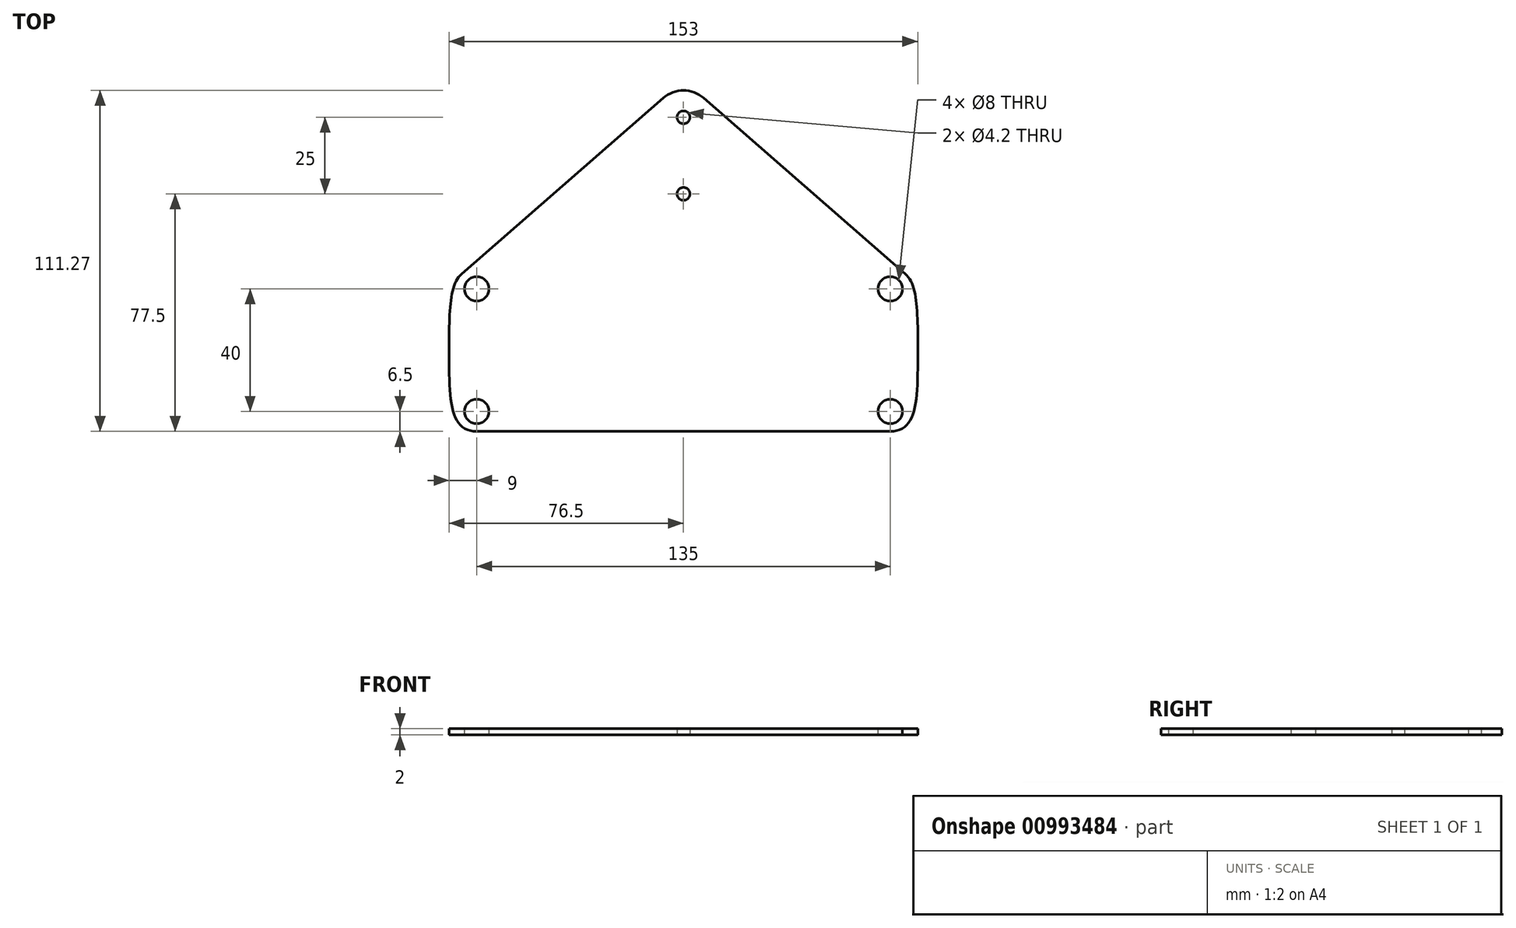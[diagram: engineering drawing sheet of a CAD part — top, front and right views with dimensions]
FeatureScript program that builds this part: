
annotation { "Feature Type Name" : "Feature", "Feature Type Description" : "" }
export const myFeature = defineFeature(function(context is Context, id is Id, definition is map)
    precondition{}
    {
        {
            var Q0;
            Q0=qCreatedBy(makeId("Top.planeOp"), FACE);
            var sketch = newSketch(context, id + "F0", { "sketchPlane" : qUnion([Q0])});
            skPoint(sketch, "E0", {"position": v(-67.5, 0) * mm});
            skPoint(sketch, "E1", {"position": v(-67.5, 40) * mm});
            skPoint(sketch, "E2", {"position": v(0, 71) * mm});
            skPoint(sketch, "E3", {"position": v(0, 96) * mm});
            skLineSegment(sketch, "E4", {"start": v(0, 0) * mm, "end": v(0, 32.96) * mm, "construction": true});
            skCircle(sketch, "E5", {"center": v(-67.5, 0) * mm, "radius": 4 * mm});
            skCircle(sketch, "E6", {"center": v(-67.5, 40) * mm, "radius": 4 * mm});
            skCircle(sketch, "E7", {"center": v(0, 71) * mm, "radius": 2.1 * mm});
            skCircle(sketch, "E8", {"center": v(0, 96) * mm, "radius": 2.1 * mm});
            skPoint(sketch, "E9", {"position": v(-67.5, 46.5) * mm});
            skPoint(sketch, "E10", {"position": v(-76.5, 20) * mm});
            skLineSegment(sketch, "E11", {"start": v(-67.5, 40) * mm, "end": v(-67.5, 0) * mm, "construction": true});
            skFitSpline(sketch, "E12", {"points": [v(-67.5, 46.5) * mm, v(-76.5, 20) * mm], "startDerivative": vector(-27, 0) * mm, "endDerivative": vector(0, -48) * mm});
            skLineSegment(sketch, "E13", {"start": v(-76.5, 20) * mm, "end": v(-53.05, 20) * mm, "construction": true});
            skLineSegment(sketch, "E14.bottom", {"start": v(-7.5, 101.5) * mm, "end": v(7.5, 101.5) * mm, "construction": true});
            skLineSegment(sketch, "E14.top", {"start": v(-7.5, 65.5) * mm, "end": v(7.5, 65.5) * mm, "construction": true});
            skLineSegment(sketch, "E14.left", {"start": v(-7.5, 101.5) * mm, "end": v(-7.5, 65.5) * mm, "construction": true});
            skLineSegment(sketch, "E14.right", {"start": v(7.5, 101.5) * mm, "end": v(7.5, 65.5) * mm, "construction": true});
            skLineSegment(sketch, "E15", {"start": v(0, 101.5) * mm, "end": v(0, 65.5) * mm, "construction": true});
            skPoint(sketch, "E15.startSnap0", {"position": v(0, 101.5) * mm});
            skLineSegment(sketch, "E16", {"start": v(-7.5, 83.5) * mm, "end": v(7.5, 83.5) * mm, "construction": true});
            skLineSegment(sketch, "E17", {"start": v(-6.57, 102.3) * mm, "end": v(-72.44, 44.85) * mm});
            skLineSegment(sketch, "E18", {"start": v(-67.5, 46.5) * mm, "end": v(0, 46.5) * mm, "construction": true});
            skFitSpline(sketch, "E19.MirrorCS", {"points": [v(-67.5, -6.5) * mm, v(-76.5, 20) * mm], "startDerivative": vector(-27, 0) * mm, "endDerivative": vector(0, 48) * mm});
            skLineSegment(sketch, "E20", {"start": v(-67.5, -6.5) * mm, "end": v(0, -6.5) * mm});
            skLineSegment(sketch, "E21.MirrorCS", {"start": v(6.57, 102.3) * mm, "end": v(72.44, 44.85) * mm});
            skFitSpline(sketch, "E22.MirrorCS", {"points": [v(67.5, 46.5) * mm, v(76.5, 20) * mm], "startDerivative": vector(27, 0) * mm, "endDerivative": vector(0, -48) * mm});
            skFitSpline(sketch, "E23.MirrorCS", {"points": [v(67.5, -6.5) * mm, v(76.5, 20) * mm], "startDerivative": vector(27, 0) * mm, "endDerivative": vector(0, 48) * mm});
            skLineSegment(sketch, "E24.MirrorCS", {"start": v(67.5, -6.5) * mm, "end": v(0, -6.5) * mm});
            skPoint(sketch, "E25.visualSharp", {"position": v(0, 108.04) * mm});
            skArc(sketch, "E25.filletArc", {"start": v(6.57, 102.3) * mm, "mid": v(0, 104.77) * mm, "end": v(-6.57, 102.3) * mm});
            skCircle(sketch, "E26.MirrorC", {"center": v(67.5, 40) * mm, "radius": 4 * mm});
            skCircle(sketch, "E27.MirrorC", {"center": v(67.5, 0) * mm, "radius": 4 * mm});
            skSolve(sketch);
        }
        {
            var Q0;
            Q0 = qSketchRegion(id + "F0", true);
            extrude(context, id + "F1", {"entities" : qUnion([Q0]), "domain" : OperationDomain.MODEL, "flatOperationType" : FlatOperationType.REMOVE, "depth" : 2 * mm, "offsetDistance" : 25 * mm});
        }
    });
